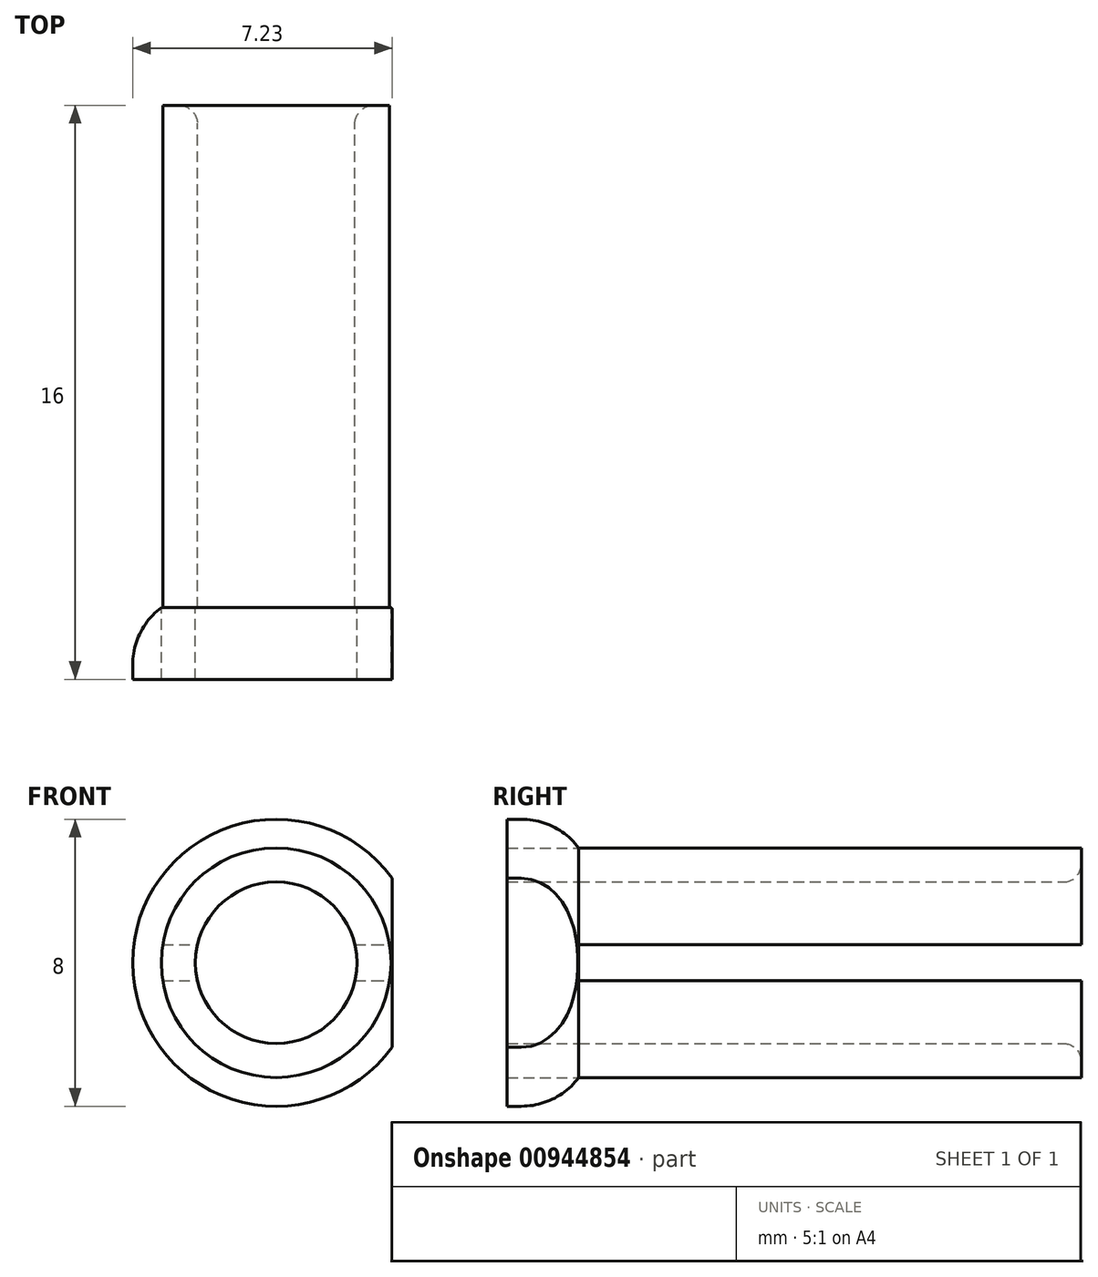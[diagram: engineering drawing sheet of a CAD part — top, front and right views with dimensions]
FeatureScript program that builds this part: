
annotation { "Feature Type Name" : "Feature", "Feature Type Description" : "" }
export const myFeature = defineFeature(function(context is Context, id is Id, definition is map)
    precondition{}
    {
        {
            var Q0;
            Q0=qCreatedBy(makeId("Front.planeOp"),FACE);
            var sketch = newSketch(context, id + "F0", { "sketchPlane" : qUnion([Q0])});
            skCircle(sketch, "E0", {"center": v(0, 0) * mm, "radius": 3.2 * mm});
            skCircle(sketch, "E1", {"center": v(0, 0) * mm, "radius": 2.25 * mm});
            skSolve(sketch);
        }
        {
            var Q0;
            Q0=makeQuery(id+"F0.imprint","IMPRINT",FACE,{"disambiguationData":[TD([[makeQuery(id+"F0.imprint","IMPRINT",EDGE,{"derivedFrom":sQuery(id+"F0.wireOp",EDGE,"E0")}),1.0]])]});
            extrude(context, id + "F1", {"entities" : qUnion([Q0]), "endBound" : BoundingType.SYMMETRIC, "depth" : 14 * mm, "offsetDistance" : 25 * mm});
        }
        {
            var Q0;
            Q0=makeQuery(id+"F1.opExtrude","CAP_EDGE",EDGE,{"disambiguationData":[OSD([sQuery(id+"F0.wireOp",EDGE,"E1")])],"isStart":true});
            fillet(context, id + "F2", {"entities" : qUnion([Q0]), "radius" : .5 * mm, "tangentPropagation" : true, "allowEdgeOverflow" : false});
        }
        {
            var Q0;
            Q0=makeQuery(id+"F1.opExtrude","CAP_FACE",FACE,{"disambiguationData":[OSD([sQuery(id+"F0.wireOp",EDGE,"E0"),sQuery(id+"F0.wireOp",EDGE,"E1")])],"isStart":false});
            var sketch = newSketch(context, id + "F3", { "sketchPlane" : qUnion([Q0])});
            skCircle(sketch, "E2", {"center": v(0, 0) * mm, "radius": 4 * mm});
            skSolve(sketch);
        }
        {
            var Q0;
            Q0=makeQuery(id+"F3.imprint","IMPRINT",FACE,{"disambiguationData":[TD([[makeQuery(id+"F3.imprint","IMPRINT",EDGE,{"derivedFrom":sQuery(id+"F3.wireOp",EDGE,"E2")}),1.0]])]});
            extrude(context, id + "F4", {"entities" : qUnion([Q0]), "operationType" : NewBodyOperationType.ADD, "depth" : 2 * mm, "offsetDistance" : 25 * mm});
        }
        {
            var Q0;
            Q0=makeQuery(id+"F4.opExtrude","CAP_EDGE",EDGE,{"disambiguationData":[OSD([sQuery(id+"F3.wireOp",EDGE,"E2")])],"isStart":true});
            fillet(context, id + "F5", {"entities" : qUnion([Q0]), "radius" : 2 * mm, "tangentPropagation" : true, "allowEdgeOverflow" : false});
        }
        {
            var Q0;
            Q0=makeQuery(id+"F1.opExtrude","CAP_FACE",FACE,{"disambiguationData":[OSD([sQuery(id+"F0.wireOp",EDGE,"E0"),sQuery(id+"F0.wireOp",EDGE,"E1")])],"isStart":false});
            extrude(context, id + "F6", {"entities" : qUnion([Q0]), "depth" : 2 * mm, "offsetDistance" : 25 * mm});
        }
        {
            var Q0;
            Q0=makeQuery(id+"F1.opExtrude","CAP_FACE",FACE,{"disambiguationData":[OSD([sQuery(id+"F0.wireOp",EDGE,"E0"),sQuery(id+"F0.wireOp",EDGE,"E1")])],"isStart":true});
            var sketch = newSketch(context, id + "F7", { "sketchPlane" : qUnion([Q0])});
            skLineSegment(sketch, "E3.bottom", {"start": v(3.62, 0.5) * mm, "end": v(-3.62, 0.5) * mm});
            skLineSegment(sketch, "E3.top", {"start": v(3.62, -0.5) * mm, "end": v(-3.62, -0.5) * mm});
            skLineSegment(sketch, "E3.left", {"start": v(3.62, 0.5) * mm, "end": v(3.62, -0.5) * mm});
            skLineSegment(sketch, "E3.right", {"start": v(-3.62, 0.5) * mm, "end": v(-3.62, -0.5) * mm});
            skPoint(sketch, "E3.middle", {"position": v(0, 0) * mm});
            skSolve(sketch);
        }
        {
            var Q0;
            {var subQ0=sQuery(id+"F7.wireOp",EDGE,"E3.right");Q0=makeQuery(id+"F7.imprint","IMPRINT",FACE,{"disambiguationData":[TD([[makeQuery(id+"F7.imprint","IMPRINT",EDGE,{"derivedFrom":subQ0}),1.0]])]});}
            var Q1;
            {var subQ0=sQuery(id+"F7.wireOp",EDGE,"E3.bottom");var subQ1=sQuery(id+"F0.wireOp",EDGE,"E0");var subQ2=makeQuery(id+"F1.opExtrude","CAP_EDGE",EDGE,{"disambiguationData":[OSD([subQ1])],"isStart":true});var subQ3=makeQuery(id+"F7.imprint","INTERSECT",VERTEX,{"disambiguationData":[OD(1.0)],"derivedFrom":[subQ2,subQ0]});Q1=makeQuery(id+"F7.imprint","IMPRINT",FACE,{"disambiguationData":[TD([[makeQuery(id+"F7.imprint","IMPRINT",EDGE,{"disambiguationData":[TD([[subQ3,1.0]])],"derivedFrom":subQ2}),-1.0]])]});}
            var Q2;
            {var subQ0=sQuery(id+"F7.wireOp",EDGE,"E3.bottom");var subQ1=sQuery(id+"F0.wireOp",EDGE,"E0");var subQ2=makeQuery(id+"F1.opExtrude","CAP_EDGE",EDGE,{"disambiguationData":[OSD([subQ1])],"isStart":true});var subQ3=makeQuery(id+"F7.imprint","INTERSECT",VERTEX,{"disambiguationData":[OD(0.0)],"derivedFrom":[subQ2,subQ0]});Q2=makeQuery(id+"F7.imprint","IMPRINT",FACE,{"disambiguationData":[TD([[makeQuery(id+"F7.imprint","IMPRINT",EDGE,{"disambiguationData":[TD([[subQ3,-1.0]])],"derivedFrom":subQ2}),-1.0]])]});}
            var Q3;
            {var subQ0=sQuery(id+"F7.wireOp",EDGE,"E3.left");Q3=makeQuery(id+"F7.imprint","IMPRINT",FACE,{"disambiguationData":[TD([[makeQuery(id+"F7.imprint","IMPRINT",EDGE,{"derivedFrom":subQ0}),-1.0]])]});}
            var Q4;
            {var subQ0=sQuery(id+"F7.wireOp",EDGE,"E3.bottom");var subQ1=sQuery(id+"F0.wireOp",EDGE,"E1");var subQ2=makeQuery(id+"F2.opFillet","BLEND_EDGE",EDGE,{"blendedFrom":[makeQuery(id+"F1.opExtrude","CAP_EDGE",EDGE,{"disambiguationData":[OSD([subQ1])],"isStart":true}),makeQuery(id+"F1.opExtrude","CAP_FACE",FACE,{"disambiguationData":[OSD([sQuery(id+"F0.wireOp",EDGE,"E0"),subQ1])],"isStart":true})],"blendedInto":[makeQuery(id+"F1.opExtrude","CAP_FACE",FACE,{"disambiguationData":[OSD([sQuery(id+"F0.wireOp",EDGE,"E0"),subQ1])],"isStart":true})]});var subQ3=makeQuery(id+"F7.imprint","INTERSECT",VERTEX,{"disambiguationData":[OD(0.0)],"derivedFrom":[subQ2,subQ0]});Q4=makeQuery(id+"F7.imprint","IMPRINT",FACE,{"disambiguationData":[TD([[makeQuery(id+"F7.imprint","IMPRINT",EDGE,{"disambiguationData":[TD([[subQ3,-1.0]])],"derivedFrom":subQ0}),1.0]])]});}
            extrude(context, id + "F8", {"entities" : qUnion([Q0, Q1, Q2, Q3, Q4]), "operationType" : NewBodyOperationType.REMOVE, "oppositeDirection" : true, "depth" : 14 * mm, "offsetDistance" : 25 * mm});
        }
        {
            var Q0;
            Q0=makeQuery(id+"F4.opExtrude","CAP_FACE",FACE,{"disambiguationData":[OSD([sQuery(id+"F0.wireOp",EDGE,"E0"),sQuery(id+"F3.wireOp",EDGE,"E2")])],"isStart":false});
            var sketch = newSketch(context, id + "F9", { "sketchPlane" : qUnion([Q0])});
            skLineSegment(sketch, "E4.bottom", {"start": v(3.23, -4.34) * mm, "end": v(4.77, -4.34) * mm});
            skLineSegment(sketch, "E4.top", {"start": v(3.23, 4.34) * mm, "end": v(4.77, 4.34) * mm});
            skLineSegment(sketch, "E4.left", {"start": v(3.23, -4.34) * mm, "end": v(3.23, 4.34) * mm});
            skLineSegment(sketch, "E4.right", {"start": v(4.77, -4.34) * mm, "end": v(4.77, 4.34) * mm});
            skPoint(sketch, "E4.middle", {"position": v(4, 0) * mm});
            skSolve(sketch);
        }
        {
            var Q0;
            {var subQ4=sQuery(id+"F9.wireOp",EDGE,"E4.bottom");Q0=makeQuery(id+"F9.imprint","IMPRINT",FACE,{"disambiguationData":[TD([[makeQuery(id+"F9.imprint","IMPRINT",EDGE,{"derivedFrom":subQ4}),1.0]])]});}
            var Q1;
            {var subQ0=sQuery(id+"F9.wireOp",EDGE,"E4.left");var subQ1=makeQuery(id+"F4.opExtrude","CAP_EDGE",EDGE,{"disambiguationData":[OSD([sQuery(id+"F3.wireOp",EDGE,"E2")])],"isStart":false});var subQ2=makeQuery(id+"F9.imprint","INTERSECT",VERTEX,{"disambiguationData":[OD(0.0)],"derivedFrom":[subQ1,subQ0]});Q1=makeQuery(id+"F9.imprint","IMPRINT",FACE,{"disambiguationData":[TD([[makeQuery(id+"F9.imprint","IMPRINT",EDGE,{"disambiguationData":[TD([[subQ2,-1.0]])],"derivedFrom":subQ0}),-1.0]])]});}
            extrude(context, id + "F10", {"entities" : qUnion([Q0, Q1]), "operationType" : NewBodyOperationType.REMOVE, "oppositeDirection" : true, "depth" : 25 * mm, "offsetDistance" : 25 * mm});
        }
    });
